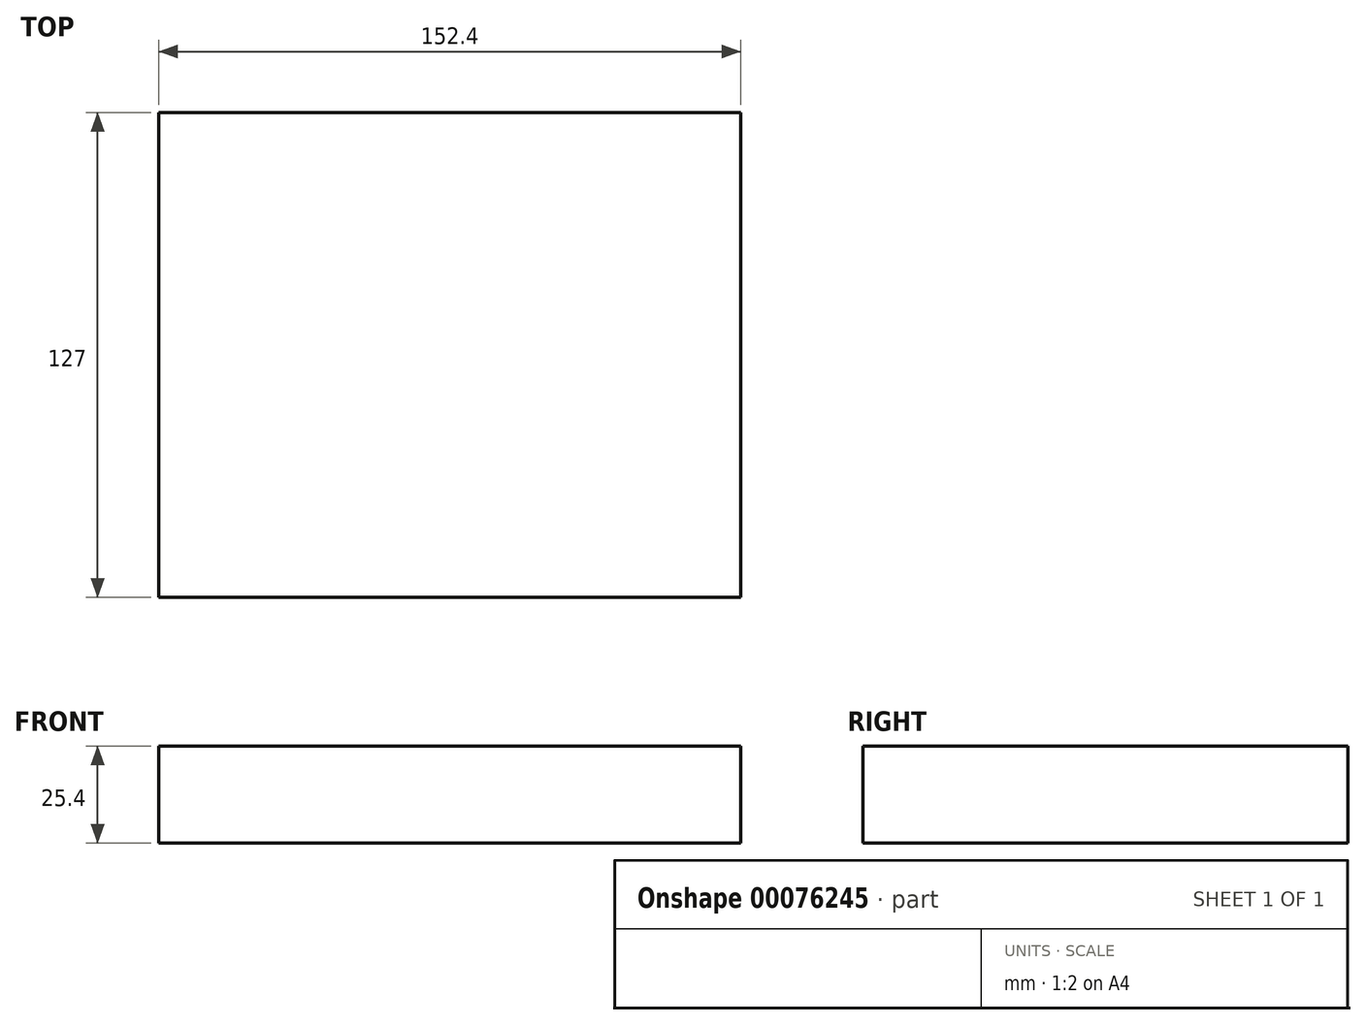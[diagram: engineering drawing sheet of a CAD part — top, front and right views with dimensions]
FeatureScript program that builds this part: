
annotation { "Feature Type Name" : "Feature", "Feature Type Description" : "" }
export const myFeature = defineFeature(function(context is Context, id is Id, definition is map)
    precondition{}
    {
        {
            var Q0;
            Q0=qCreatedBy(makeId("Right.planeOp"),FACE);
            var sketch = newSketch(context, id + "F0", { "sketchPlane" : qUnion([Q0])});
            skLineSegment(sketch, "E0.bottom", {"start": v(-127, 25.4) * mm, "end": v(0, 25.4) * mm});
            skLineSegment(sketch, "E0.top", {"start": v(-127, 0) * mm, "end": v(0, 0) * mm});
            skLineSegment(sketch, "E0.left", {"start": v(-127, 25.4) * mm, "end": v(-127, 0) * mm});
            skLineSegment(sketch, "E0.right", {"start": v(0, 25.4) * mm, "end": v(0, 0) * mm});
            skSolve(sketch);
        }
        {
            var Q0;
            Q0=makeQuery(id+"F0.imprint","IMPRINT",FACE,{"disambiguationData":[TD([[makeQuery(id+"F0.imprint","IMPRINT",EDGE,{"derivedFrom":sQuery(id+"F0.wireOp",EDGE,"E0.bottom")}),-1.0]])]});
            extrude(context, id + "F1", {"entities" : qUnion([Q0]), "depth" : 152.4 * mm});
        }
    });
